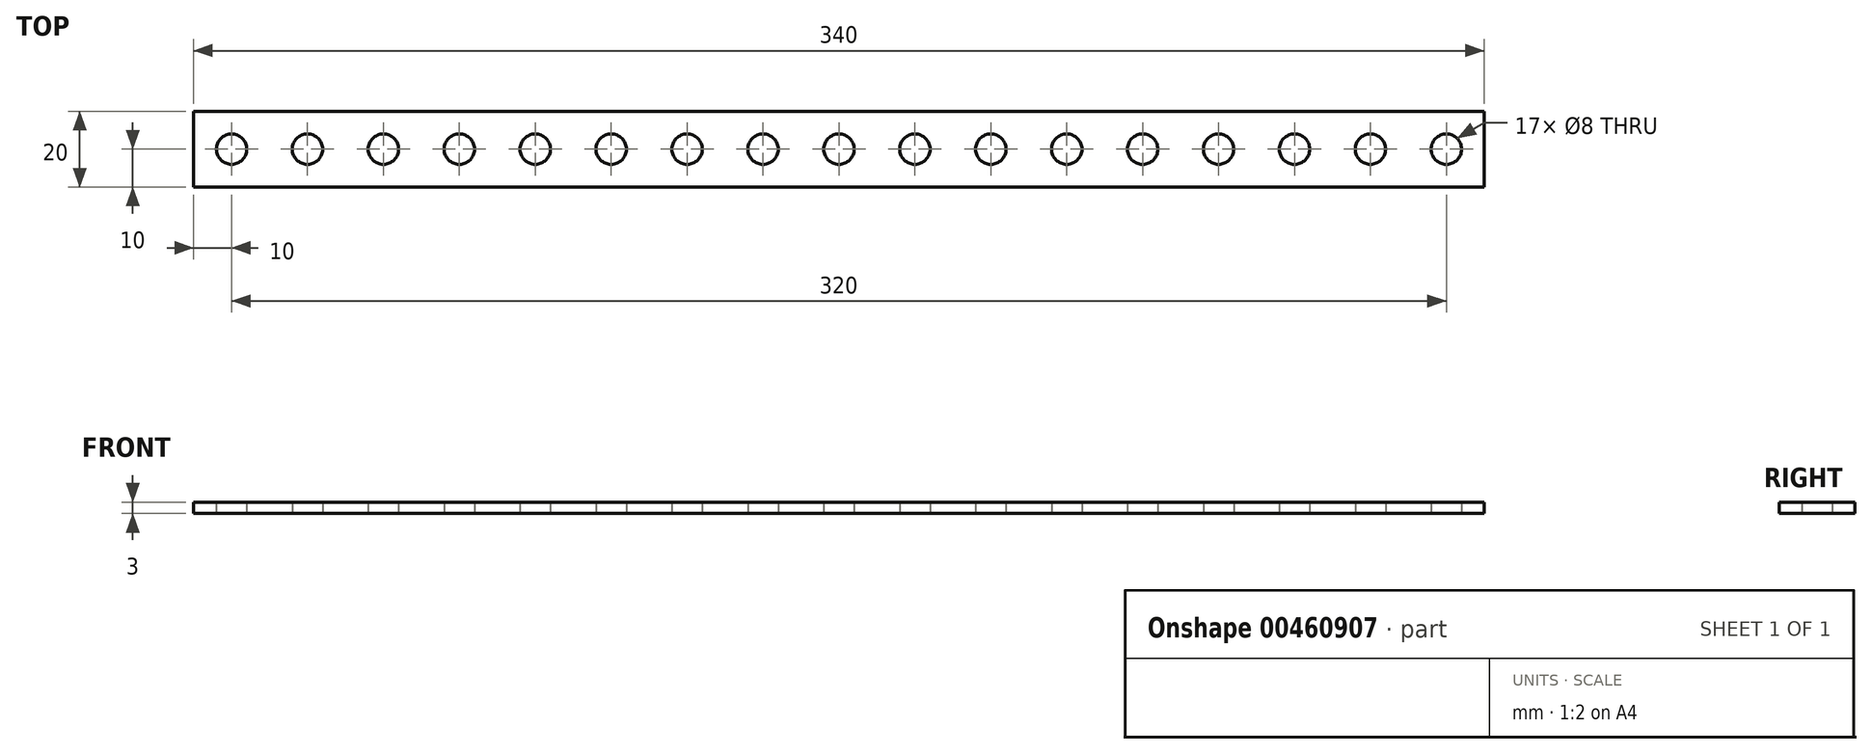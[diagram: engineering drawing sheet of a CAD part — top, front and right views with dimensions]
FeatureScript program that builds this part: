
annotation { "Feature Type Name" : "Feature", "Feature Type Description" : "" }
export const myFeature = defineFeature(function(context is Context, id is Id, definition is map)
    precondition{}
    {
        {
            var Q0;
            Q0=qCreatedBy(makeId("Top.planeOp"),FACE);
            var sketch = newSketch(context, id + "F0", { "sketchPlane" : qUnion([Q0])});
            skLineSegment(sketch, "E0.bottom", {"start": v(170, 10) * mm, "end": v(-170, 10) * mm});
            skLineSegment(sketch, "E0.top", {"start": v(170, -10) * mm, "end": v(-170, -10) * mm});
            skLineSegment(sketch, "E0.left", {"start": v(170, 10) * mm, "end": v(170, -10) * mm});
            skLineSegment(sketch, "E0.right", {"start": v(-170, 10) * mm, "end": v(-170, -10) * mm});
            skPoint(sketch, "E0.middle", {"position": v(0, 0) * mm});
            skCircle(sketch, "E1", {"center": v(-160, 0) * mm, "radius": 4 * mm});
            skPoint(sketch, "E1.centerSnap0", {"position": v(-170, 0) * mm});
            skCircle(sketch, "E2.1.0.0", {"center": v(-140, 0) * mm, "radius": 4 * mm});
            skCircle(sketch, "E2.2.0.0", {"center": v(-120, 0) * mm, "radius": 4 * mm});
            skCircle(sketch, "E2.3.0.0", {"center": v(-100, 0) * mm, "radius": 4 * mm});
            skCircle(sketch, "E2.4.0.0", {"center": v(-80, 0) * mm, "radius": 4 * mm});
            skCircle(sketch, "E2.5.0.0", {"center": v(-60, 0) * mm, "radius": 4 * mm});
            skCircle(sketch, "E2.6.0.0", {"center": v(-40, 0) * mm, "radius": 4 * mm});
            skCircle(sketch, "E2.7.0.0", {"center": v(-20, 0) * mm, "radius": 4 * mm});
            skCircle(sketch, "E2.8.0.0", {"center": v(0, 0) * mm, "radius": 4 * mm});
            skCircle(sketch, "E2.9.0.0", {"center": v(20, 0) * mm, "radius": 4 * mm});
            skCircle(sketch, "E2.10.0.0", {"center": v(40, 0) * mm, "radius": 4 * mm});
            skCircle(sketch, "E2.11.0.0", {"center": v(60, 0) * mm, "radius": 4 * mm});
            skCircle(sketch, "E2.12.0.0", {"center": v(80, 0) * mm, "radius": 4 * mm});
            skCircle(sketch, "E2.13.0.0", {"center": v(100, 0) * mm, "radius": 4 * mm});
            skCircle(sketch, "E2.14.0.0", {"center": v(120, 0) * mm, "radius": 4 * mm});
            skCircle(sketch, "E2.15.0.0", {"center": v(140, 0) * mm, "radius": 4 * mm});
            skCircle(sketch, "E2.16.0.0", {"center": v(160, 0) * mm, "radius": 4 * mm});
            skLineSegment(sketch, "E2.direction1", {"start": v(-160, 0) * mm, "end": v(-140, 0) * mm, "construction": true});
            skSolve(sketch);
        }
        {
            var Q0;
            Q0=makeQuery(id+"F0.imprint","IMPRINT",FACE,{"disambiguationData":[TD([[makeQuery(id+"F0.imprint","IMPRINT",EDGE,{"derivedFrom":sQuery(id+"F0.wireOp",EDGE,"E0.bottom")}),1.0]])]});
            extrude(context, id + "F1", {"entities" : qUnion([Q0]), "depth" : 3 * mm, "offsetDistance" : 25 * mm});
        }
    });
